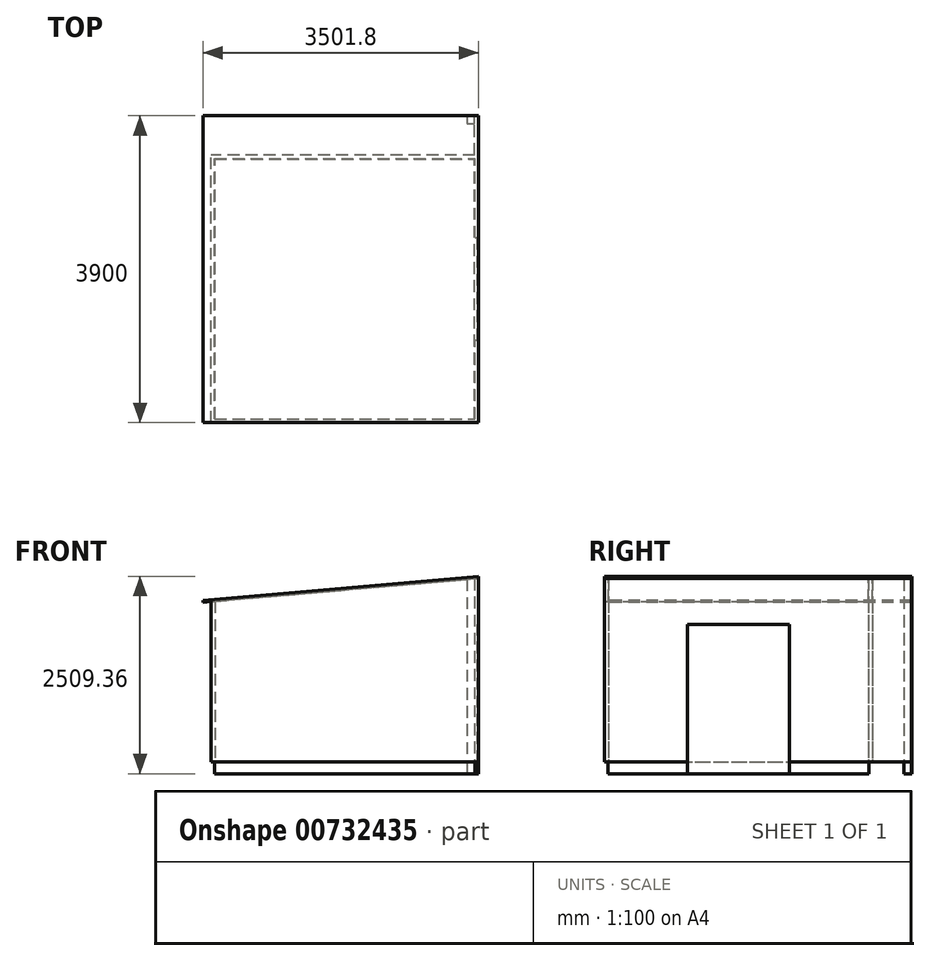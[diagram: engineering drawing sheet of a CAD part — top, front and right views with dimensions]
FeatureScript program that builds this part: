
annotation { "Feature Type Name" : "Feature", "Feature Type Description" : "" }
export const myFeature = defineFeature(function(context is Context, id is Id, definition is map)
    precondition{}
    {
        {
            var Q0;
            Q0=qCreatedBy(makeId("Top.planeOp"),FACE);
            var sketch = newSketch(context, id + "F0", { "sketchPlane" : qUnion([Q0])});
            skLineSegment(sketch, "E0.bottom", {"start": v(0, 0) * mm, "end": v(3400, 0) * mm});
            skLineSegment(sketch, "E0.top", {"start": v(0, 3400) * mm, "end": v(3350, 3400) * mm});
            skLineSegment(sketch, "E0.left", {"start": v(0, 0) * mm, "end": v(0, 3400) * mm});
            skLineSegment(sketch, "E0.right", {"start": v(3400, 0) * mm, "end": v(3400, 3400) * mm});
            skLineSegment(sketch, "E1.0", {"start": v(50, 3350) * mm, "end": v(3350, 3350) * mm});
            skLineSegment(sketch, "E1.1", {"start": v(50, 50) * mm, "end": v(50, 3350) * mm});
            skLineSegment(sketch, "E1.2", {"start": v(50, 50) * mm, "end": v(3350, 50) * mm});
            skLineSegment(sketch, "E1.3", {"start": v(3350, 50) * mm, "end": v(3350, 3350) * mm});
            skLineSegment(sketch, "E2.0", {"start": v(250, 3150) * mm, "end": v(3150, 3150) * mm});
            skLineSegment(sketch, "E2.1", {"start": v(250, 250) * mm, "end": v(250, 3150) * mm});
            skLineSegment(sketch, "E2.2", {"start": v(250, 250) * mm, "end": v(3150, 250) * mm});
            skLineSegment(sketch, "E2.3", {"start": v(3150, 250) * mm, "end": v(3150, 3150) * mm});
            skLineSegment(sketch, "E3.bottom", {"start": v(3250, 3900) * mm, "end": v(3350, 3900) * mm});
            skLineSegment(sketch, "E3.top", {"start": v(3250, 3800) * mm, "end": v(3350, 3800) * mm});
            skLineSegment(sketch, "E3.left", {"start": v(3250, 3900) * mm, "end": v(3250, 3800) * mm});
            skLineSegment(sketch, "E3.right", {"start": v(3350, 3900) * mm, "end": v(3350, 3800) * mm});
            skLineSegment(sketch, "E4", {"start": v(3400, 3400) * mm, "end": v(3400, 3899.85) * mm});
            skLineSegment(sketch, "E5", {"start": v(3350, 3900) * mm, "end": v(3350, 3400) * mm});
            skLineSegment(sketch, "E6", {"start": v(3350, 3900) * mm, "end": v(3400, 3899.85) * mm});
            skSolve(sketch);
        }
        {
            var Q0;
            Q0=sQuery(id+"F0.wireOp",EDGE,"E0.right");
            cPlane(context, id + "F1", {"entities" : qUnion([Q0]), "cplaneType" : CPlaneType.LINE_ANGLE, "offset" : 25 * mm, "angle" : 5 * degree, "oppositeDirection" : true, "width" : 150 * mm, "height" : 150 * mm});
        }
        {
            var Q0;
            Q0=qCreatedBy(id+"F1.planeOp",FACE);
            cPlane(context, id + "F2", {"entities" : qUnion([Q0]), "cplaneType" : CPlaneType.OFFSET, "offset" : 2475 * mm, "width" : 150 * mm, "height" : 150 * mm});
        }
        {
            var Q0;
            Q0=makeQuery(id+"F0.imprint","IMPRINT",FACE,{"disambiguationData":[TD([[makeQuery(id+"F0.imprint","IMPRINT",EDGE,{"derivedFrom":sQuery(id+"F0.wireOp",EDGE,"E0.bottom")}),1.0]])]});
            var Q1;
            Q1=qCreatedBy(id+"F2.planeOp",FACE);
            extrude(context, id + "F3", {"entities" : qUnion([Q0]), "endBound" : BoundingType.UP_TO_SURFACE, "depth" : 25 * mm, "endBoundEntityFace" : qUnion([Q1]), "offsetDistance" : 25 * mm});
        }
        {
            var Q0;
            Q0=qCreatedBy(id+"F2.planeOp",FACE);
            var sketch = newSketch(context, id + "F4", { "sketchPlane" : qUnion([Q0])});
            skLineSegment(sketch, "E7.bottom", {"start": v(90.6, 0) * mm, "end": v(3603.6, 0) * mm});
            skLineSegment(sketch, "E7.top", {"start": v(90.6, 3900) * mm, "end": v(3603.6, 3900) * mm});
            skLineSegment(sketch, "E7.left", {"start": v(90.6, 3900) * mm, "end": v(90.6, 0) * mm});
            skLineSegment(sketch, "E7.right", {"start": v(3603.6, 3900) * mm, "end": v(3603.6, 0) * mm});
            skSolve(sketch);
        }
        {
            var Q0;
            Q0=makeQuery(id+"F4.imprint","IMPRINT",FACE,{"disambiguationData":[TD([[makeQuery(id+"F4.imprint","IMPRINT",EDGE,{"derivedFrom":sQuery(id+"F4.wireOp",EDGE,"E7.bottom")}),1.0]])]});
            extrude(context, id + "F5", {"entities" : qUnion([Q0]), "operationType" : NewBodyOperationType.ADD, "depth" : 25 * mm, "offsetDistance" : 25 * mm});
        }
        {
            var Q0;
            Q0=makeQuery(id+"F0.imprint","IMPRINT",FACE,{"disambiguationData":[TD([[makeQuery(id+"F0.imprint","IMPRINT",EDGE,{"derivedFrom":sQuery(id+"F0.wireOp",EDGE,"E3.bottom")}),-1.0]])]});
            var Q1;
            {var subQ0=sQuery(id+"F4.wireOp",EDGE,"E7.top");var subQ1=sQuery(id+"F4.wireOp",EDGE,"E7.left");var subQ2=sQuery(id+"F4.wireOp",EDGE,"E7.bottom");var subQ3=sQuery(id+"F4.wireOp",EDGE,"E7.right");Q1=makeQuery(id+"F5.boolean.opBoolean","SPLIT",FACE,{"disambiguationData":[TD([makeQuery(id+"F3.opExtrude","SWEPT_FACE",FACE,{"disambiguationData":[OSD([sQuery(id+"F0.wireOp",EDGE,"E0.bottom")])]})])],"derivedFrom":makeQuery(id+"F5.opExtrude","CAP_FACE",FACE,{"disambiguationData":[OSD([subQ2,subQ0,subQ1,subQ3])],"isStart":true})});}
            extrude(context, id + "F6", {"entities" : qUnion([Q0]), "operationType" : NewBodyOperationType.ADD, "endBound" : BoundingType.UP_TO_SURFACE, "depth" : 25 * mm, "endBoundEntityFace" : qUnion([Q1]), "offsetDistance" : 25 * mm});
        }
        {
            var Q0;
            Q0=makeQuery(id+"F3.opExtrude","SWEPT_FACE",FACE,{"disambiguationData":[OSD([sQuery(id+"F0.wireOp",EDGE,"E0.right"),sQuery(id+"F0.wireOp",EDGE,"E4")])]});
            var sketch = newSketch(context, id + "F7", { "sketchPlane" : qUnion([Q0])});
            skLineSegment(sketch, "E8.bottom", {"start": v(1050, 0) * mm, "end": v(2350, 0) * mm});
            skLineSegment(sketch, "E8.top", {"start": v(1050, 1900) * mm, "end": v(2350, 1900) * mm});
            skLineSegment(sketch, "E8.left", {"start": v(1050, 0) * mm, "end": v(1050, 1900) * mm});
            skLineSegment(sketch, "E8.right", {"start": v(2350, 0) * mm, "end": v(2350, 1900) * mm});
            skLineSegment(sketch, "E9", {"start": v(1450, 1900) * mm, "end": v(1450, 0) * mm});
            skLineSegment(sketch, "E10", {"start": v(0, 150) * mm, "end": v(1050, 150) * mm});
            skLineSegment(sketch, "E11.0.1.0", {"start": v(0, 275) * mm, "end": v(1050, 275) * mm});
            skLineSegment(sketch, "E11.0.2.0", {"start": v(0, 400) * mm, "end": v(1050, 400) * mm});
            skLineSegment(sketch, "E11.0.3.0", {"start": v(0, 525) * mm, "end": v(1050, 525) * mm});
            skLineSegment(sketch, "E11.0.4.0", {"start": v(0, 650) * mm, "end": v(1050, 650) * mm});
            skLineSegment(sketch, "E11.0.5.0", {"start": v(0, 775) * mm, "end": v(1050, 775) * mm});
            skLineSegment(sketch, "E11.0.6.0", {"start": v(0, 900) * mm, "end": v(1050, 900) * mm});
            skLineSegment(sketch, "E11.0.7.0", {"start": v(0, 1025) * mm, "end": v(1050, 1025) * mm});
            skLineSegment(sketch, "E11.0.8.0", {"start": v(0, 1150) * mm, "end": v(1050, 1150) * mm});
            skLineSegment(sketch, "E11.0.9.0", {"start": v(0, 1275) * mm, "end": v(1050, 1275) * mm});
            skLineSegment(sketch, "E11.0.10.0", {"start": v(0, 1400) * mm, "end": v(1050, 1400) * mm});
            skLineSegment(sketch, "E11.0.11.0", {"start": v(0, 1525) * mm, "end": v(1050, 1525) * mm});
            skLineSegment(sketch, "E11.0.12.0", {"start": v(0, 1650) * mm, "end": v(1050, 1650) * mm});
            skLineSegment(sketch, "E11.0.13.0", {"start": v(0, 1775) * mm, "end": v(1050, 1775) * mm});
            skLineSegment(sketch, "E11.0.14.0", {"start": v(0, 1900) * mm, "end": v(3899.85, 1900) * mm});
            skLineSegment(sketch, "E11.0.15.0", {"start": v(0, 2025) * mm, "end": v(1050, 2025) * mm});
            skLineSegment(sketch, "E11.0.16.0", {"start": v(0, 2150) * mm, "end": v(1050, 2150) * mm});
            skLineSegment(sketch, "E11.0.17.0", {"start": v(0, 2275) * mm, "end": v(1050, 2275) * mm});
            skLineSegment(sketch, "E11.direction1", {"start": v(0, 150) * mm, "end": v(1, 150) * mm, "construction": true});
            skLineSegment(sketch, "E11.direction2", {"start": v(0, 150) * mm, "end": v(0, 275) * mm, "construction": true});
            skLineSegment(sketch, "E12", {"start": v(0, 2359.36) * mm, "end": v(3899.85, 2359.36) * mm});
            skLineSegment(sketch, "E13.trimOffspring", {"start": v(2350, 1775) * mm, "end": v(3899.85, 1775) * mm});
            skLineSegment(sketch, "E14.trimOffspring", {"start": v(2350, 1650) * mm, "end": v(3899.85, 1650) * mm});
            skLineSegment(sketch, "E15.trimOffspring", {"start": v(2350, 1525) * mm, "end": v(3899.85, 1525) * mm});
            skLineSegment(sketch, "E16.trimOffspring", {"start": v(2350, 1400) * mm, "end": v(3899.85, 1400) * mm});
            skLineSegment(sketch, "E17.trimOffspring", {"start": v(2350, 1275) * mm, "end": v(3899.85, 1275) * mm});
            skLineSegment(sketch, "E18.trimOffspring", {"start": v(2350, 1150) * mm, "end": v(3899.85, 1150) * mm});
            skLineSegment(sketch, "E19.trimOffspring", {"start": v(2350, 1025) * mm, "end": v(3899.85, 1025) * mm});
            skLineSegment(sketch, "E20.trimOffspring", {"start": v(2350, 900) * mm, "end": v(3899.85, 900) * mm});
            skLineSegment(sketch, "E21.trimOffspring", {"start": v(2350, 775) * mm, "end": v(3899.85, 775) * mm});
            skLineSegment(sketch, "E22.trimOffspring", {"start": v(2350, 650) * mm, "end": v(3899.85, 650) * mm});
            skLineSegment(sketch, "E23.trimOffspring", {"start": v(2350, 525) * mm, "end": v(3899.85, 525) * mm});
            skLineSegment(sketch, "E24.trimOffspring", {"start": v(2350, 400) * mm, "end": v(3899.85, 400) * mm});
            skLineSegment(sketch, "E25.trimOffspring", {"start": v(2350, 275) * mm, "end": v(3899.85, 275) * mm});
            skLineSegment(sketch, "E26.trimOffspring", {"start": v(2350, 150) * mm, "end": v(3899.85, 150) * mm});
            skLineSegment(sketch, "E27", {"start": v(3354.85, 0) * mm, "end": v(3354.85, 150) * mm});
            skLineSegment(sketch, "E28.top", {"start": v(1050, 2300) * mm, "end": v(2350, 2300) * mm});
            skLineSegment(sketch, "E28.left", {"start": v(1050, 1900) * mm, "end": v(1050, 2300) * mm});
            skLineSegment(sketch, "E28.right", {"start": v(2350, 1900) * mm, "end": v(2350, 2300) * mm});
            skLineSegment(sketch, "E29.trimOffspring", {"start": v(2350, 2150) * mm, "end": v(3899.85, 2150) * mm});
            skLineSegment(sketch, "E30.trimOffspring", {"start": v(2350, 2025) * mm, "end": v(3899.85, 2025) * mm});
            skLineSegment(sketch, "E31.trimOffspring", {"start": v(2350, 2275) * mm, "end": v(3899.85, 2275) * mm});
            skSolve(sketch);
        }
        {
            var Q0;
            {var subQ0=sQuery(id+"F7.wireOp",EDGE,"E8.right");Q0=makeQuery(id+"F7.imprint","IMPRINT",FACE,{"disambiguationData":[TD([[makeQuery(id+"F7.imprint","IMPRINT",EDGE,{"derivedFrom":subQ0}),1.0]])]});}
            var Q1;
            {var subQ0=sQuery(id+"F7.wireOp",EDGE,"E8.left");Q1=makeQuery(id+"F7.imprint","IMPRINT",FACE,{"disambiguationData":[TD([[makeQuery(id+"F7.imprint","IMPRINT",EDGE,{"derivedFrom":subQ0}),-1.0]])]});}
            extrude(context, id + "F8", {"entities" : qUnion([Q0, Q1]), "operationType" : NewBodyOperationType.REMOVE, "oppositeDirection" : true, "depth" : 15 * mm, "offsetDistance" : 25 * mm});
        }
        {
            var Q0;
            Q0=makeQuery(id+"F5.boolean.opBoolean","MERGE",FACE,{"derivedFrom":[makeQuery(id+"F3.opExtrude","SWEPT_FACE",FACE,{"disambiguationData":[OSD([sQuery(id+"F0.wireOp",EDGE,"E0.bottom")])]}),makeQuery(id+"F5.opExtrude","SWEPT_FACE",FACE,{"disambiguationData":[OSD([sQuery(id+"F4.wireOp",EDGE,"E7.bottom")])]})]});
            var sketch = newSketch(context, id + "F9", { "sketchPlane" : qUnion([Q0])});
            skLineSegment(sketch, "E32", {"start": v(0, 150) * mm, "end": v(3400, 150) * mm});
            skLineSegment(sketch, "E33", {"start": v(0, 275) * mm, "end": v(3400, 275) * mm});
            skLineSegment(sketch, "E34.0.1.0", {"start": v(0, 400) * mm, "end": v(3400, 400) * mm});
            skLineSegment(sketch, "E34.0.2.0", {"start": v(0, 525) * mm, "end": v(3400, 525) * mm});
            skLineSegment(sketch, "E34.0.3.0", {"start": v(0, 650) * mm, "end": v(3400, 650) * mm});
            skLineSegment(sketch, "E34.0.4.0", {"start": v(0, 775) * mm, "end": v(3400, 775) * mm});
            skLineSegment(sketch, "E34.0.5.0", {"start": v(0, 900) * mm, "end": v(3400, 900) * mm});
            skLineSegment(sketch, "E34.0.6.0", {"start": v(0, 1025) * mm, "end": v(3400, 1025) * mm});
            skLineSegment(sketch, "E34.0.7.0", {"start": v(0, 1150) * mm, "end": v(3400, 1150) * mm});
            skLineSegment(sketch, "E34.0.8.0", {"start": v(0, 1275) * mm, "end": v(3400, 1275) * mm});
            skLineSegment(sketch, "E34.0.9.0", {"start": v(0, 1400) * mm, "end": v(3400, 1400) * mm});
            skLineSegment(sketch, "E34.0.10.0", {"start": v(0, 1525) * mm, "end": v(3400, 1525) * mm});
            skLineSegment(sketch, "E34.0.11.0", {"start": v(0, 1650) * mm, "end": v(3400, 1650) * mm});
            skLineSegment(sketch, "E34.0.12.0", {"start": v(0, 1775) * mm, "end": v(3400, 1775) * mm});
            skLineSegment(sketch, "E34.0.13.0", {"start": v(0, 1900) * mm, "end": v(3400, 1900) * mm});
            skLineSegment(sketch, "E34.0.14.0", {"start": v(0, 2025) * mm, "end": v(3400, 2025) * mm});
            skLineSegment(sketch, "E34.0.15.0", {"start": v(1011.39, 2150) * mm, "end": v(3400, 2150) * mm});
            skLineSegment(sketch, "E34.direction1", {"start": v(0, 275) * mm, "end": v(0, 275) * mm});
            skLineSegment(sketch, "E34.direction2", {"start": v(0, 275) * mm, "end": v(0, 400) * mm, "construction": true});
            skLineSegment(sketch, "E35", {"start": v(3400, 2275) * mm, "end": v(2440.14, 2275) * mm});
            skLineSegment(sketch, "E36.0", {"start": v(0, 2061.52) * mm, "end": v(3400, 2358.98) * mm});
            skPoint(sketch, "E37.orphan", {"position": v(0, 2150) * mm});
            skSolve(sketch);
        }
        {
            var Q0;
            Q0=makeQuery(id+"F3.opExtrude","SWEPT_FACE",FACE,{"disambiguationData":[OSD([sQuery(id+"F0.wireOp",EDGE,"E0.left")])]});
            var sketch = newSketch(context, id + "F10", { "sketchPlane" : qUnion([Q0])});
            skLineSegment(sketch, "E38", {"start": v(0, 150) * mm, "end": v(-3400, 150) * mm});
            skLineSegment(sketch, "E39.0.1.0", {"start": v(0, 275) * mm, "end": v(-3400, 275) * mm});
            skLineSegment(sketch, "E39.0.2.0", {"start": v(0, 400) * mm, "end": v(-3400, 400) * mm});
            skLineSegment(sketch, "E39.0.3.0", {"start": v(0, 525) * mm, "end": v(-3400, 525) * mm});
            skLineSegment(sketch, "E39.0.4.0", {"start": v(0, 650) * mm, "end": v(-3400, 650) * mm});
            skLineSegment(sketch, "E39.0.5.0", {"start": v(0, 775) * mm, "end": v(-3400, 775) * mm});
            skLineSegment(sketch, "E39.0.6.0", {"start": v(0, 900) * mm, "end": v(-3400, 900) * mm});
            skLineSegment(sketch, "E39.0.7.0", {"start": v(0, 1025) * mm, "end": v(-3400, 1025) * mm});
            skLineSegment(sketch, "E39.0.8.0", {"start": v(0, 1150) * mm, "end": v(-3400, 1150) * mm});
            skLineSegment(sketch, "E39.0.9.0", {"start": v(0, 1275) * mm, "end": v(-3400, 1275) * mm});
            skLineSegment(sketch, "E39.0.10.0", {"start": v(0, 1400) * mm, "end": v(-3400, 1400) * mm});
            skLineSegment(sketch, "E39.0.11.0", {"start": v(0, 1525) * mm, "end": v(-3400, 1525) * mm});
            skLineSegment(sketch, "E39.0.12.0", {"start": v(0, 1650) * mm, "end": v(-3400, 1650) * mm});
            skLineSegment(sketch, "E39.0.13.0", {"start": v(0, 1775) * mm, "end": v(-3400, 1775) * mm});
            skLineSegment(sketch, "E39.0.14.0", {"start": v(0, 1900) * mm, "end": v(-3400, 1900) * mm});
            skLineSegment(sketch, "E39.0.15.0", {"start": v(0, 2025) * mm, "end": v(-3400, 2025) * mm});
            skLineSegment(sketch, "E39.direction1", {"start": v(-3400, 150) * mm, "end": v(-3400, 150) * mm});
            skLineSegment(sketch, "E39.direction2", {"start": v(-3400, 150) * mm, "end": v(-3400, 275) * mm, "construction": true});
            skSolve(sketch);
        }
        {
            var Q0;
            Q0 = qSketchRegion(id + "F10", true);
            var Q1;
            {var subQ0=sQuery(id+"F10.wireOp",EDGE,"E38");Q1=makeQuery(id+"F10.imprint","IMPRINT",FACE,{"disambiguationData":[TD([[makeQuery(id+"F10.imprint","IMPRINT",EDGE,{"derivedFrom":subQ0}),1.0]])]});}
            extrude(context, id + "F11", {"entities" : qUnion([Q0, Q1]), "operationType" : NewBodyOperationType.REMOVE, "oppositeDirection" : true, "depth" : 45 * mm, "offsetDistance" : 25 * mm});
        }
        {
            var Q0;
            Q0 = qSketchRegion(id + "F9", true);
            var Q1;
            {var subQ0=sQuery(id+"F9.wireOp",EDGE,"E32");Q1=makeQuery(id+"F9.imprint","IMPRINT",FACE,{"disambiguationData":[TD([[makeQuery(id+"F9.imprint","IMPRINT",EDGE,{"derivedFrom":subQ0}),-1.0]])]});}
            extrude(context, id + "F12", {"entities" : qUnion([Q0, Q1]), "operationType" : NewBodyOperationType.REMOVE, "oppositeDirection" : true, "depth" : 45 * mm, "offsetDistance" : 25 * mm});
        }
        {
            var Q0;
            Q0=makeQuery(id+"F3.opExtrude","SWEPT_FACE",FACE,{"disambiguationData":[OSD([sQuery(id+"F0.wireOp",EDGE,"E0.top")])]});
            var sketch = newSketch(context, id + "F13", { "sketchPlane" : qUnion([Q0])});
            skLineSegment(sketch, "E40", {"start": v(0, 150) * mm, "end": v(-3350, 150) * mm});
            skLineSegment(sketch, "E41.0.1.0", {"start": v(0, 275) * mm, "end": v(-3350, 275) * mm});
            skLineSegment(sketch, "E41.0.2.0", {"start": v(0, 400) * mm, "end": v(-3350, 400) * mm});
            skLineSegment(sketch, "E41.0.3.0", {"start": v(0, 525) * mm, "end": v(-3350, 525) * mm});
            skLineSegment(sketch, "E41.0.4.0", {"start": v(0, 650) * mm, "end": v(-3350, 650) * mm});
            skLineSegment(sketch, "E41.0.5.0", {"start": v(0, 775) * mm, "end": v(-3350, 775) * mm});
            skLineSegment(sketch, "E41.0.6.0", {"start": v(0, 900) * mm, "end": v(-3350, 900) * mm});
            skLineSegment(sketch, "E41.0.7.0", {"start": v(0, 1025) * mm, "end": v(-3350, 1025) * mm});
            skLineSegment(sketch, "E41.0.8.0", {"start": v(0, 1150) * mm, "end": v(-3350, 1150) * mm});
            skLineSegment(sketch, "E41.0.9.0", {"start": v(0, 1275) * mm, "end": v(-3350, 1275) * mm});
            skLineSegment(sketch, "E41.0.10.0", {"start": v(0, 1400) * mm, "end": v(-3350, 1400) * mm});
            skLineSegment(sketch, "E41.0.11.0", {"start": v(0, 1525) * mm, "end": v(-3350, 1525) * mm});
            skLineSegment(sketch, "E41.0.12.0", {"start": v(0, 1650) * mm, "end": v(-3350, 1650) * mm});
            skLineSegment(sketch, "E41.0.13.0", {"start": v(0, 1775) * mm, "end": v(-3350, 1775) * mm});
            skLineSegment(sketch, "E41.0.14.0", {"start": v(0, 1900) * mm, "end": v(-3350, 1900) * mm});
            skLineSegment(sketch, "E41.0.15.0", {"start": v(0, 2025) * mm, "end": v(-3350, 2025) * mm});
            skLineSegment(sketch, "E41.0.16.0", {"start": v(0, 2150) * mm, "end": v(-3350, 2150) * mm});
            skLineSegment(sketch, "E41.direction1", {"start": v(-3350, 150) * mm, "end": v(-3350, 150) * mm});
            skLineSegment(sketch, "E41.direction2", {"start": v(-3350, 150) * mm, "end": v(-3350, 275) * mm, "construction": true});
            skLineSegment(sketch, "E42", {"start": v(-3350, 2275) * mm, "end": v(-1005.93, 2275) * mm});
            skLineSegment(sketch, "E43", {"start": v(-3350, 2400) * mm, "end": v(-2434.69, 2400) * mm});
            skSolve(sketch);
        }
        {
            var Q0;
            Q0 = qSketchRegion(id + "F13", true);
            var Q1;
            {var subQ1=sQuery(id+"F0.wireOp",EDGE,"E0.top");var subQ5=makeQuery(id+"F3.opExtrude","CAP_EDGE",EDGE,{"disambiguationData":[OSD([subQ1])],"isStart":true});Q1=makeQuery(id+"F13.imprint","IMPRINT",FACE,{"disambiguationData":[TD([[makeQuery(id+"F13.imprint","IMPRINT",EDGE,{"derivedFrom":subQ5}),-1.0]])]});}
            extrude(context, id + "F14", {"entities" : qUnion([Q0, Q1]), "operationType" : NewBodyOperationType.REMOVE, "oppositeDirection" : true, "depth" : 45 * mm, "offsetDistance" : 25 * mm});
        }
        {
            var Q0;
            {var subQ4=sQuery(id+"F7.wireOp",EDGE,"E10");Q0=makeQuery(id+"F7.imprint","IMPRINT",FACE,{"disambiguationData":[TD([[makeQuery(id+"F7.imprint","IMPRINT",EDGE,{"derivedFrom":subQ4}),-1.0]])]});}
            extrude(context, id + "F15", {"entities" : qUnion([Q0]), "operationType" : NewBodyOperationType.REMOVE, "oppositeDirection" : true, "depth" : 45 * mm, "offsetDistance" : 25 * mm});
        }
        {
            var Q0;
            {var subQ5=sQuery(id+"F7.wireOp",EDGE,"E27");Q0=makeQuery(id+"F7.imprint","IMPRINT",FACE,{"disambiguationData":[TD([[makeQuery(id+"F7.imprint","IMPRINT",EDGE,{"derivedFrom":subQ5}),1.0]])]});}
            extrude(context, id + "F16", {"entities" : qUnion([Q0]), "operationType" : NewBodyOperationType.REMOVE, "oppositeDirection" : true, "depth" : 45 * mm, "offsetDistance" : 25 * mm});
        }
        {
            var Q0;
            {var subQ4=sQuery(id+"F7.wireOp",EDGE,"E27");Q0=makeQuery(id+"F7.imprint","IMPRINT",FACE,{"disambiguationData":[TD([[makeQuery(id+"F7.imprint","IMPRINT",EDGE,{"derivedFrom":subQ4}),-1.0]])]});}
            extrude(context, id + "F17", {"entities" : qUnion([Q0]), "operationType" : NewBodyOperationType.REMOVE, "oppositeDirection" : true, "depth" : 50 * mm, "offsetDistance" : 25 * mm});
        }
    });
